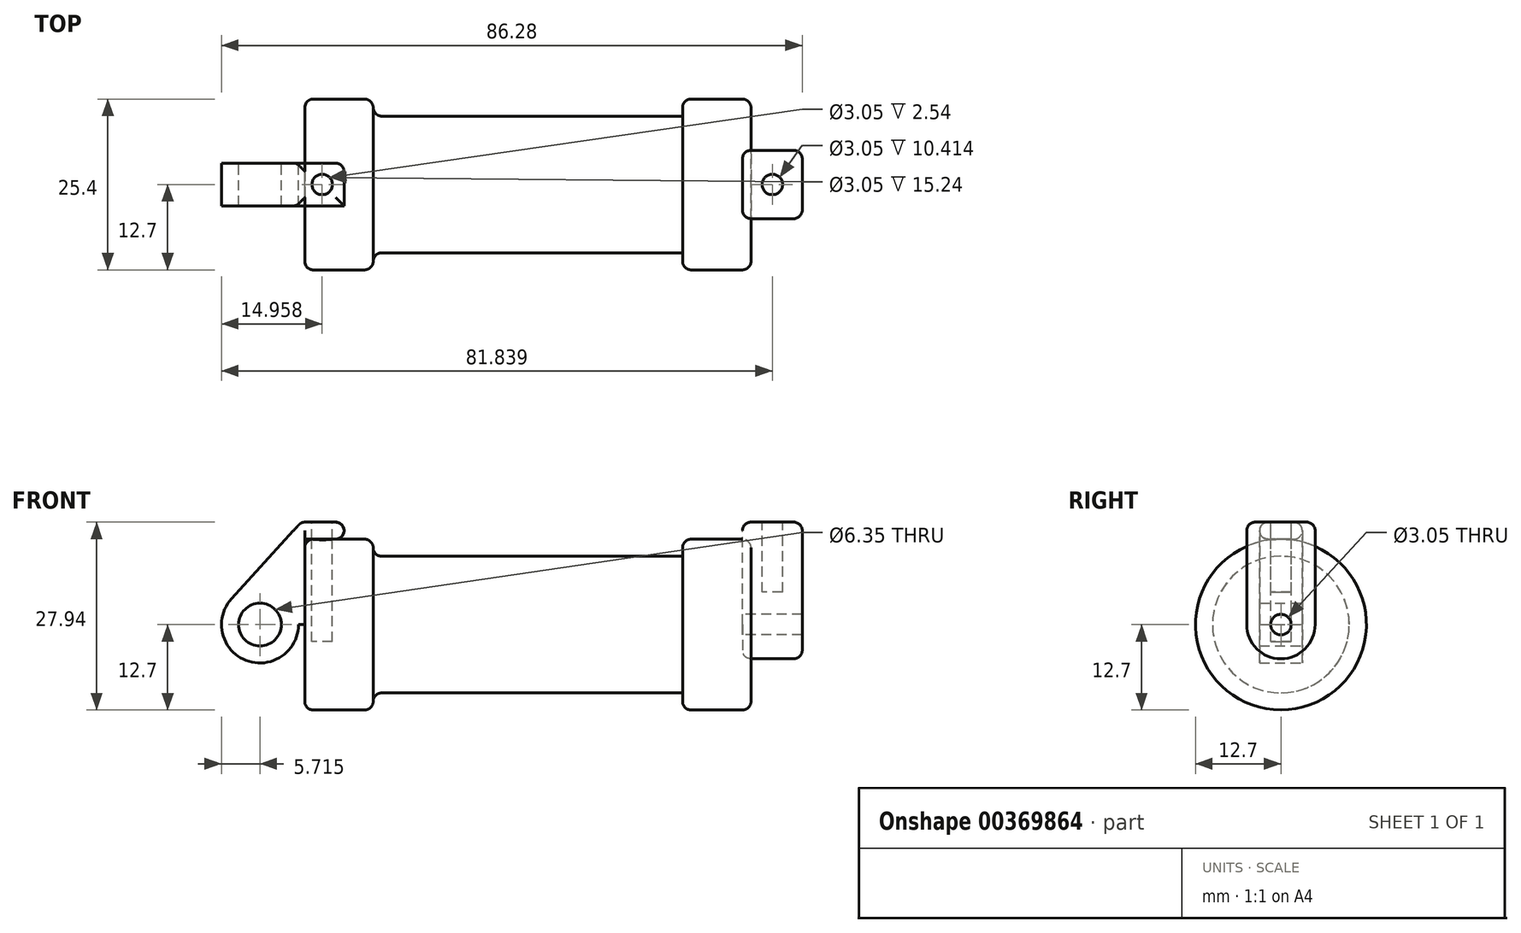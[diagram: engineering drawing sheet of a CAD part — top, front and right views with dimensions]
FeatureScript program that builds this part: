
annotation { "Feature Type Name" : "Feature", "Feature Type Description" : "" }
export const myFeature = defineFeature(function(context is Context, id is Id, definition is map)
    precondition{}
    {
        {
            var Q0;
            Q0=qCreatedBy(makeId("Front.planeOp"),FACE);
            var sketch = newSketch(context, id + "F0", { "sketchPlane" : qUnion([Q0])});
            skLineSegment(sketch, "E0", {"start": v(0, 0) * mm, "end": v(0, 12.7) * mm});
            skLineSegment(sketch, "E1", {"start": v(0, 12.7) * mm, "end": v(10.16, 12.7) * mm});
            skLineSegment(sketch, "E2", {"start": v(10.16, 12.7) * mm, "end": v(10.16, 10.16) * mm});
            skLineSegment(sketch, "E3", {"start": v(10.16, 10.16) * mm, "end": v(56.13, 10.16) * mm});
            skLineSegment(sketch, "E4", {"start": v(56.13, 10.16) * mm, "end": v(56.13, 12.7) * mm});
            skLineSegment(sketch, "E5", {"start": v(56.13, 12.7) * mm, "end": v(66.3, 12.7) * mm});
            skLineSegment(sketch, "E6", {"start": v(66.3, 12.7) * mm, "end": v(66.3, 0) * mm});
            skLineSegment(sketch, "E7", {"start": v(66.3, 0) * mm, "end": v(0, 0) * mm});
            skLineSegment(sketch, "E8", {"start": v(5.84, 15.24) * mm, "end": v(-0.5, 15.24) * mm});
            skLineSegment(sketch, "E9", {"start": v(-0.5, 15.24) * mm, "end": v(-10.88, 3.85) * mm});
            skLineSegment(sketch, "E10", {"start": v(0, 0) * mm, "end": v(-6.65, 0) * mm});
            skCircle(sketch, "E11", {"center": v(-6.65, 0) * mm, "radius": 5.72 * mm});
            skCircle(sketch, "E12", {"center": v(-6.65, 0) * mm, "radius": 3.18 * mm});
            skLineSegment(sketch, "E13", {"start": v(5.84, 15.24) * mm, "end": v(5.84, -9.4) * mm});
            skLineSegment(sketch, "E14", {"start": v(5.84, -9.4) * mm, "end": v(-8.18, -5.5) * mm});
            skSolve(sketch);
        }
        {
            var Q0;
            {var subQ0=sQuery(id+"F0.wireOp",EDGE,"E2");Q0=makeQuery(id+"F0.imprint","IMPRINT",FACE,{"disambiguationData":[TD([[makeQuery(id+"F0.imprint","IMPRINT",EDGE,{"derivedFrom":subQ0}),-1.0]])]});}
            var Q1;
            {var subQ0=sQuery(id+"F0.wireOp",EDGE,"E0");Q1=makeQuery(id+"F0.imprint","IMPRINT",FACE,{"disambiguationData":[TD([[makeQuery(id+"F0.imprint","IMPRINT",EDGE,{"derivedFrom":subQ0}),-1.0]])]});}
            var Q2;
            Q2=sQuery(id+"F0.wireOp",EDGE,"E7");
            revolve(context, id + "F1", {"entities" : qUnion([Q0, Q1]), "axis" : qUnion([Q2]), "revolveType" : RevolveType.FULL});
        }
        {
            var Q0;
            {var subQ1=sQuery(id+"F0.wireOp",EDGE,"E0");Q0=makeQuery(id+"F0.imprint","IMPRINT",FACE,{"disambiguationData":[TD([[makeQuery(id+"F0.imprint","IMPRINT",EDGE,{"derivedFrom":subQ1}),1.0]])]});}
            var Q1;
            {var subQ5=sQuery(id+"F0.wireOp",EDGE,"E12");Q1=makeQuery(id+"F0.imprint","IMPRINT",FACE,{"disambiguationData":[TD([[makeQuery(id+"F0.imprint","IMPRINT",EDGE,{"derivedFrom":subQ5}),-1.0]])]});}
            extrude(context, id + "F2", {"entities" : qUnion([Q0, Q1]), "endBound" : BoundingType.SYMMETRIC, "depth" : 6.35 * mm});
        }
        {
            var Q0;
            Q0=makeQuery(id+"F1.opRevolve","SWEPT_FACE",FACE,{"disambiguationData":[OSD([sQuery(id+"F0.wireOp",EDGE,"E6")])]});
            var sketch = newSketch(context, id + "F3", { "sketchPlane" : qUnion([Q0])});
            skCircle(sketch, "E15", {"center": v(0, 0) * mm, "radius": 1.52 * mm});
            skCircle(sketch, "E16", {"center": v(0, 0) * mm, "radius": 5.08 * mm});
            skLineSegment(sketch, "E17", {"start": v(-5.08, 0) * mm, "end": v(5.08, 0) * mm, "construction": true});
            skLineSegment(sketch, "E18", {"start": v(5.08, 0) * mm, "end": v(5.08, 15.24) * mm});
            skLineSegment(sketch, "E19", {"start": v(5.08, 15.24) * mm, "end": v(0.06, 15.24) * mm});
            skLineSegment(sketch, "E20", {"start": v(-5.08, 0) * mm, "end": v(-5.08, 15.24) * mm});
            skLineSegment(sketch, "E21", {"start": v(-5.08, 15.24) * mm, "end": v(0.06, 15.24) * mm});
            skSolve(sketch);
        }
        {
            var Q0;
            Q0 = qSketchRegion(id + "F3", true);
            extrude(context, id + "F4", {"entities" : qUnion([Q0]), "depth" : 7.62 * mm, "hasSecondDirection" : true, "secondDirectionOppositeDirection" : true, "secondDirectionDepth" : 1.27 * mm});
        }
        {
            var Q0;
            Q0=makeQuery(id+"F4.opExtrude","SWEPT_FACE",FACE,{"disambiguationData":[OSD([sQuery(id+"F3.wireOp",EDGE,"E19"),sQuery(id+"F3.wireOp",EDGE,"E21")])]});
            var sketch = newSketch(context, id + "F5", { "sketchPlane" : qUnion([Q0])});
            skLineSegment(sketch, "E22", {"start": v(65.02, 0) * mm, "end": v(73.91, 0) * mm, "construction": true});
            skCircle(sketch, "E23", {"center": v(69.47, 0) * mm, "radius": 1.52 * mm});
            skSolve(sketch);
        }
        {
            var Q0;
            Q0=makeQuery(id+"F2.opExtrude","SWEPT_FACE",FACE,{"disambiguationData":[OSD([sQuery(id+"F0.wireOp",EDGE,"E8")])]});
            var sketch = newSketch(context, id + "F6", { "sketchPlane" : qUnion([Q0])});
            skCircle(sketch, "E24", {"center": v(2.59, 0) * mm, "radius": 1.52 * mm});
            skPoint(sketch, "E24.centerSnap0", {"position": v(5.84, 0) * mm});
            skSolve(sketch);
        }
        {
            var Q0;
            Q0 = qSketchRegion(id + "F6", true);
            extrude(context, id + "F7", {"entities" : qUnion([Q0]), "operationType" : NewBodyOperationType.REMOVE, "oppositeDirection" : true, "depth" : 17.78 * mm});
        }
        {
            var Q0;
            Q0 = qSketchRegion(id + "F5", true);
            extrude(context, id + "F8", {"entities" : qUnion([Q0]), "operationType" : NewBodyOperationType.REMOVE, "oppositeDirection" : true, "depth" : 10.4 * mm});
        }
        {
            var Q0;
            Q0=makeQuery(id+"F2.opExtrude","CAP_EDGE",EDGE,{"disambiguationData":[OSD([sQuery(id+"F0.wireOp",EDGE,"E8")])],"isStart":true});
            var Q1;
            Q1=makeQuery(id+"F2.opExtrude","SWEPT_EDGE",EDGE,{"disambiguationData":[OSD([sQuery(id+"F0.wireOp",EDGE,"E8"),sQuery(id+"F0.wireOp",EDGE,"E9")])]});
            var Q2;
            Q2=makeQuery(id+"F2.opExtrude","SWEPT_EDGE",EDGE,{"disambiguationData":[OSD([sQuery(id+"F0.wireOp",EDGE,"E8"),sQuery(id+"F0.wireOp",EDGE,"E13")])]});
            var Q3;
            Q3=makeQuery(id+"F2.opExtrude","CAP_EDGE",EDGE,{"disambiguationData":[OSD([sQuery(id+"F0.wireOp",EDGE,"E8")])],"isStart":false});
            var Q4;
            Q4=makeQuery(id+"F1.opRevolve","SWEPT_EDGE",EDGE,{"disambiguationData":[OSD([sQuery(id+"F0.wireOp",EDGE,"E1"),sQuery(id+"F0.wireOp",EDGE,"E2")])]});
            var Q5;
            Q5=makeQuery(id+"F1.opRevolve","SWEPT_EDGE",EDGE,{"disambiguationData":[OSD([sQuery(id+"F0.wireOp",EDGE,"E0"),sQuery(id+"F0.wireOp",EDGE,"E1")])]});
            var Q6;
            Q6=makeQuery(id+"F2.opExtrude","SWEPT_EDGE",EDGE,{"disambiguationData":[OSD([sQuery(id+"F0.wireOp",EDGE,"E1"),sQuery(id+"F0.wireOp",EDGE,"E13")])]});
            var Q7;
            Q7=makeQuery(id+"F2.opExtrude","CAP_EDGE",EDGE,{"disambiguationData":[OSD([sQuery(id+"F0.wireOp",EDGE,"E1")])],"isStart":false});
            var Q8;
            Q8=makeQuery(id+"F2.opExtrude","CAP_EDGE",EDGE,{"disambiguationData":[OSD([sQuery(id+"F0.wireOp",EDGE,"E1")])],"isStart":true});
            var Q9;
            Q9=makeQuery(id+"F2.opExtrude","CAP_EDGE",EDGE,{"disambiguationData":[OSD([sQuery(id+"F0.wireOp",EDGE,"E13")])],"isStart":true});
            var Q10;
            Q10=makeQuery(id+"F1.opRevolve","SWEPT_EDGE",EDGE,{"disambiguationData":[OSD([sQuery(id+"F0.wireOp",EDGE,"E2"),sQuery(id+"F0.wireOp",EDGE,"E3")])]});
            fillet(context, id + "F9", {"entities" : qUnion([Q0, Q1, Q2, Q3, Q4, Q5, Q6, Q7, Q8, Q9, Q10]), "radius" : 1.27 * mm, "tangentPropagation" : true, "allowEdgeOverflow" : false});
        }
        {
            var Q0;
            Q0=makeQuery(id+"F1.opRevolve","SWEPT_EDGE",EDGE,{"disambiguationData":[OSD([sQuery(id+"F0.wireOp",EDGE,"E5"),sQuery(id+"F0.wireOp",EDGE,"E6")])]});
            var Q1;
            Q1=makeQuery(id+"F1.opRevolve","SWEPT_EDGE",EDGE,{"disambiguationData":[OSD([sQuery(id+"F0.wireOp",EDGE,"E4"),sQuery(id+"F0.wireOp",EDGE,"E5")])]});
            var Q2;
            Q2=makeQuery(id+"F4.opExtrude","SWEPT_FACE",FACE,{"disambiguationData":[OSD([sQuery(id+"F3.wireOp",EDGE,"E20")])]});
            var Q3;
            Q3=makeQuery(id+"F4.opExtrude","CAP_EDGE",EDGE,{"disambiguationData":[OSD([sQuery(id+"F3.wireOp",EDGE,"E19"),sQuery(id+"F3.wireOp",EDGE,"E21")])],"isStart":false});
            var Q4;
            Q4=makeQuery(id+"F4.opExtrude","SWEPT_EDGE",EDGE,{"disambiguationData":[OSD([sQuery(id+"F3.wireOp",EDGE,"E18"),sQuery(id+"F3.wireOp",EDGE,"E19")])]});
            var Q5;
            Q5=makeQuery(id+"F4.opExtrude","CAP_EDGE",EDGE,{"disambiguationData":[OSD([sQuery(id+"F3.wireOp",EDGE,"E19"),sQuery(id+"F3.wireOp",EDGE,"E21")])],"isStart":true});
            fillet(context, id + "F10", {"entities" : qUnion([Q0, Q1, Q2, Q3, Q4, Q5]), "radius" : 1.27 * mm, "tangentPropagation" : true, "allowEdgeOverflow" : false});
        }
    });
